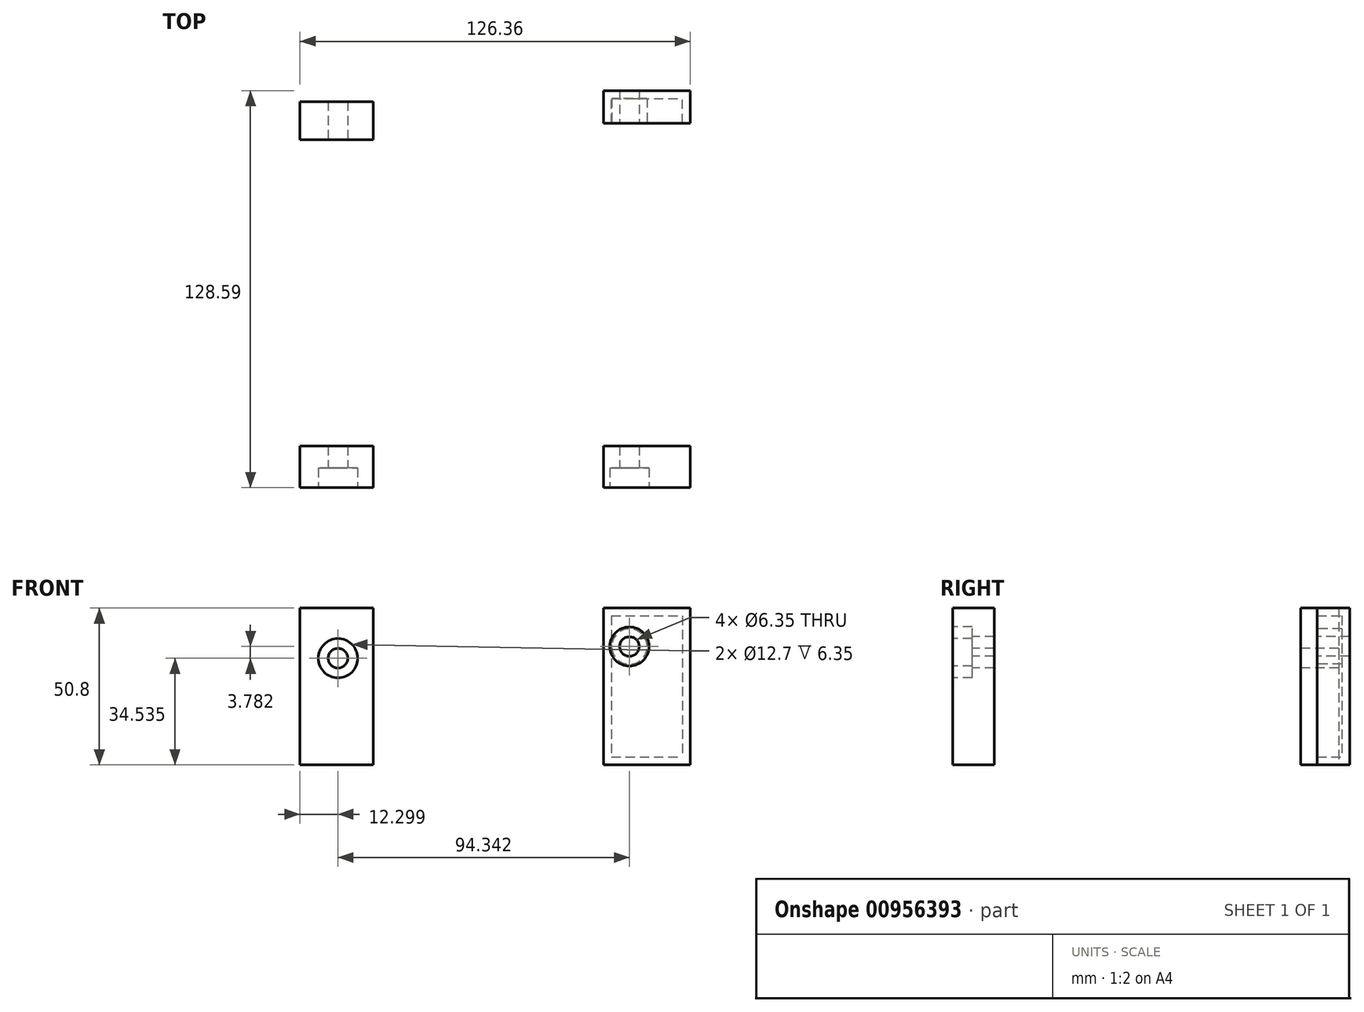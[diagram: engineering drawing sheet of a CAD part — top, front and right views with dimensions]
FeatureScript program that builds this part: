
annotation { "Feature Type Name" : "Feature", "Feature Type Description" : "" }
export const myFeature = defineFeature(function(context is Context, id is Id, definition is map)
    precondition{}
    {
        {
            var Q0;
            Q0=qCreatedBy(makeId("Top.planeOp"),FACE);
            var sketch = newSketch(context, id + "F0", { "sketchPlane" : qUnion([Q0])});
            skLineSegment(sketch, "E0.bottom", {"start": v(-62.72, -54.07) * mm, "end": v(-38.96, -54.07) * mm});
            skLineSegment(sketch, "E0.top", {"start": v(-62.72, -67.53) * mm, "end": v(-38.96, -67.53) * mm});
            skLineSegment(sketch, "E0.left", {"start": v(-62.72, -54.07) * mm, "end": v(-62.72, -67.53) * mm});
            skLineSegment(sketch, "E0.right", {"start": v(-38.96, -54.07) * mm, "end": v(-38.96, -67.53) * mm});
            skLineSegment(sketch, "E1.bottom", {"start": v(35.56, -54.07) * mm, "end": v(63.64, -54.07) * mm});
            skLineSegment(sketch, "E1.top", {"start": v(35.56, -67.53) * mm, "end": v(63.64, -67.53) * mm});
            skLineSegment(sketch, "E1.left", {"start": v(35.56, -54.07) * mm, "end": v(35.56, -67.53) * mm});
            skLineSegment(sketch, "E1.right", {"start": v(63.64, -54.07) * mm, "end": v(63.64, -67.53) * mm});
            skLineSegment(sketch, "E2.bottom", {"start": v(-62.72, 57.46) * mm, "end": v(-38.96, 57.46) * mm});
            skLineSegment(sketch, "E2.top", {"start": v(-62.72, 45.14) * mm, "end": v(-38.96, 45.14) * mm});
            skLineSegment(sketch, "E2.left", {"start": v(-62.72, 57.46) * mm, "end": v(-62.72, 45.14) * mm});
            skLineSegment(sketch, "E2.right", {"start": v(-38.96, 57.46) * mm, "end": v(-38.96, 45.14) * mm});
            skLineSegment(sketch, "E3.bottom", {"start": v(35.56, 50.5) * mm, "end": v(63.64, 50.5) * mm});
            skLineSegment(sketch, "E3.top", {"start": v(35.56, 61.06) * mm, "end": v(63.64, 61.06) * mm});
            skLineSegment(sketch, "E3.left", {"start": v(35.56, 50.5) * mm, "end": v(35.56, 61.06) * mm});
            skLineSegment(sketch, "E3.right", {"start": v(63.64, 50.5) * mm, "end": v(63.64, 61.06) * mm});
            skSolve(sketch);
        }
        {
            var Q0;
            Q0=makeQuery(id+"F0.imprint","IMPRINT",FACE,{"disambiguationData":[TD([[makeQuery(id+"F0.imprint","IMPRINT",EDGE,{"derivedFrom":sQuery(id+"F0.wireOp",EDGE,"E2.bottom")}),-1.0]])]});
            var Q1;
            Q1=makeQuery(id+"F0.imprint","IMPRINT",FACE,{"disambiguationData":[TD([[makeQuery(id+"F0.imprint","IMPRINT",EDGE,{"derivedFrom":sQuery(id+"F0.wireOp",EDGE,"E0.bottom")}),-1.0]])]});
            var Q2;
            Q2=makeQuery(id+"F0.imprint","IMPRINT",FACE,{"disambiguationData":[TD([[makeQuery(id+"F0.imprint","IMPRINT",EDGE,{"derivedFrom":sQuery(id+"F0.wireOp",EDGE,"E1.bottom")}),-1.0]])]});
            var Q3;
            Q3=makeQuery(id+"F0.imprint","IMPRINT",FACE,{"disambiguationData":[TD([[makeQuery(id+"F0.imprint","IMPRINT",EDGE,{"derivedFrom":sQuery(id+"F0.wireOp",EDGE,"E3.bottom")}),1.0]])]});
            extrude(context, id + "F1", {"entities" : qUnion([Q0, Q1, Q2, Q3]), "depth" : 50.8 * mm, "offsetDistance" : 25.4 * mm});
        }
        {
            var Q0;
            Q0=makeQuery(id+"F1.opExtrude","SWEPT_FACE",FACE,{"disambiguationData":[OSD([sQuery(id+"F0.wireOp",EDGE,"E0.top")])]});
            var sketch = newSketch(context, id + "F2", { "sketchPlane" : qUnion([Q0])});
            skCircle(sketch, "E4", {"center": v(-50.42, 34.54) * mm, "radius": 10.54 * mm});
            skCircle(sketch, "E5", {"center": v(8.2, 107.43) * mm, "radius": 4.93 * mm});
            skCircle(sketch, "E6", {"center": v(115.6, 112.31) * mm, "radius": 10 * mm});
            skCircle(sketch, "E7", {"center": v(43.92, 38.32) * mm, "radius": 8.53 * mm});
            skSolve(sketch);
        }
        {
            var Q0;
            Q0=sQuery(id+"F2.wireOp",VERTEX,"E5.center");
            var Q1;
            Q1=sQuery(id+"F2.wireOp",VERTEX,"E4.center");
            var Q2;
            Q2=sQuery(id+"F2.wireOp",VERTEX,"E7.center");
            var Q3;
            Q3=sQuery(id+"F2.wireOp",VERTEX,"E6.center");
            var Q4;
            Q4=makeQuery(id+"F1.opExtrude","SWEPT_BODY",BODY,{"disambiguationData":[OSD([sQuery(id+"F0.wireOp",EDGE,"E0.bottom"),sQuery(id+"F0.wireOp",EDGE,"E0.top"),sQuery(id+"F0.wireOp",EDGE,"E0.left"),sQuery(id+"F0.wireOp",EDGE,"E0.right")])]});
            var Q5;
            Q5=makeQuery(id+"F1.opExtrude","SWEPT_BODY",BODY,{"disambiguationData":[OSD([sQuery(id+"F0.wireOp",EDGE,"E1.bottom"),sQuery(id+"F0.wireOp",EDGE,"E1.top"),sQuery(id+"F0.wireOp",EDGE,"E1.left"),sQuery(id+"F0.wireOp",EDGE,"E1.right")])]});
            var Q6;
            Q6=makeQuery(id+"F1.opExtrude","SWEPT_BODY",BODY,{"disambiguationData":[OSD([sQuery(id+"F0.wireOp",EDGE,"E2.bottom"),sQuery(id+"F0.wireOp",EDGE,"E2.top"),sQuery(id+"F0.wireOp",EDGE,"E2.left"),sQuery(id+"F0.wireOp",EDGE,"E2.right")])]});
            var Q7;
            Q7=makeQuery(id+"F1.opExtrude","SWEPT_BODY",BODY,{"disambiguationData":[OSD([sQuery(id+"F0.wireOp",EDGE,"E3.bottom"),sQuery(id+"F0.wireOp",EDGE,"E3.top"),sQuery(id+"F0.wireOp",EDGE,"E3.left"),sQuery(id+"F0.wireOp",EDGE,"E3.right")])]});
            hole(context, id + "F3", {"style" : HoleStyle.C_BORE, "endStyle" : HoleEndStyle.THROUGH, "holeDiameter" : 6.35 * mm, "cBoreDiameter" : 12.7 * mm, "cBoreDepth" : 6.35 * mm, "majorDiameter" : 6.35 * mm, "isTappedThrough" : true, "tappedDepth" : 12.7 * mm, "tapClearance" : 3, "locations" : qUnion([Q0, Q1, Q2, Q3]), "scope" : qUnion([Q4, Q5, Q6, Q7])});
        }
        {
            var Q0;
            Q0=makeQuery(id+"F1.opExtrude","SWEPT_FACE",FACE,{"disambiguationData":[OSD([sQuery(id+"F0.wireOp",EDGE,"E3.bottom")])]});
            shell(context, id + "F4", {"entities" : qUnion([Q0]), "thickness" : 2.54 * mm});
        }
    });
